AUTODESK INVENTOR PART (.ipt)
format: ipt  version: 2023 (Build 270158000, 158)  size: 151,552 bytes
history: native  units: mm
features: extrude x2, sketch x2
ambient origin geometry x8: Origin, YZ Plane, XZ Plane, XY Plane, X Axis, Y Axis, Z Axis, Center Point
bodies: Solid1 (feature_tree)
feature tree (4):
  extrude  "Extrusion1"  Depth=92.0mm
  extrude  "Extrusion2"  Depth=100.0mm
  sketch  "Sketch1"  dims[d0=15.0mm d1=92.0mm]
  sketch  "Sketch2"  dims[d2=40.0mm d3=100.0mm d4=120.0mm d5=0.0mm d6=65.0mm d7=18.0mm d8=20.0mm d9=0.0mm]
